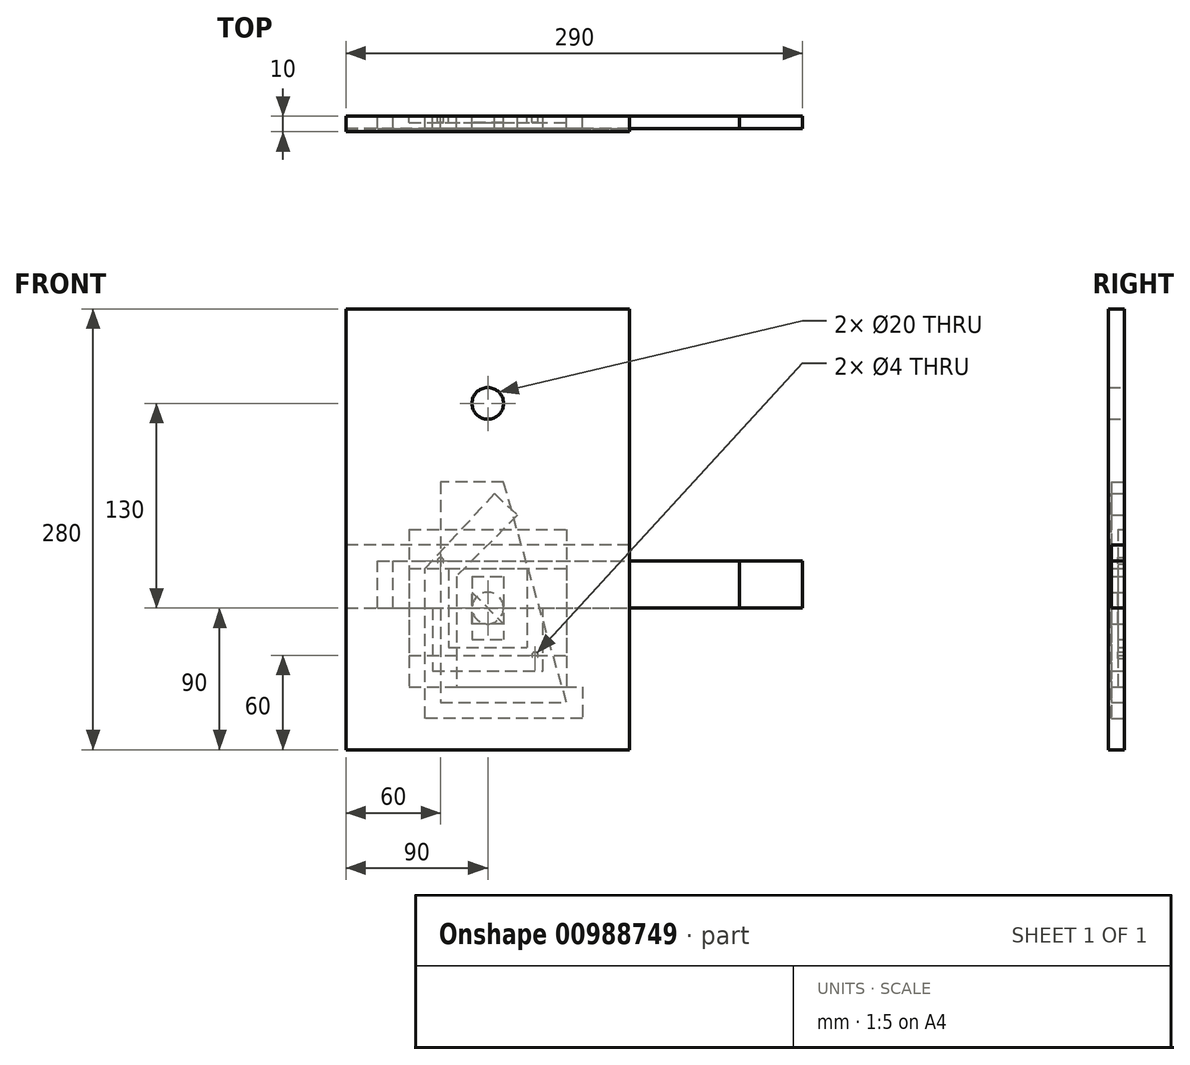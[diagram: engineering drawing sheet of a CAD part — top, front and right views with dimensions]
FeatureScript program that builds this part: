
annotation { "Feature Type Name" : "Feature", "Feature Type Description" : "" }
export const myFeature = defineFeature(function(context is Context, id is Id, definition is map)
    precondition{}
    {
        {
            var Q0;
            Q0=qCreatedBy(makeId("Front.planeOp"),FACE);
            var sketch = newSketch(context, id + "F0", { "sketchPlane" : qUnion([Q0])});
            skLineSegment(sketch, "E0", {"start": v(-30, -60) * mm, "end": v(50, -60) * mm});
            skLineSegment(sketch, "E1", {"start": v(50, -60) * mm, "end": v(10, 80) * mm});
            skLineSegment(sketch, "E2", {"start": v(10, 80) * mm, "end": v(-30, 80) * mm});
            skLineSegment(sketch, "E3", {"start": v(-30, 80) * mm, "end": v(-30, -60) * mm});
            skSolve(sketch);
        }
        {
            var Q0;
            Q0=makeQuery(id+"F0.imprint","IMPRINT",FACE,{"disambiguationData":[TD([[makeQuery(id+"F0.imprint","IMPRINT",EDGE,{"derivedFrom":sQuery(id+"F0.wireOp",EDGE,"E0")}),1.0]])]});
            extrude(context, id + "F1", {"entities" : qUnion([Q0]), "depth" : 8 * mm, "offsetDistance" : 25 * mm});
        }
        {
            var Q0;
            Q0=qCreatedBy(makeId("Front.planeOp"),FACE);
            var sketch = newSketch(context, id + "F2", { "sketchPlane" : qUnion([Q0])});
            skLineSegment(sketch, "E4.bottom", {"start": v(-60, 0) * mm, "end": v(160, 0) * mm});
            skLineSegment(sketch, "E4.top", {"start": v(-60, 30) * mm, "end": v(160, 30) * mm});
            skLineSegment(sketch, "E4.left", {"start": v(-60, 0) * mm, "end": v(-60, 30) * mm});
            skLineSegment(sketch, "E4.right", {"start": v(160, 0) * mm, "end": v(160, 30) * mm});
            skSolve(sketch);
        }
        {
            var Q0;
            Q0=makeQuery(id+"F2.imprint","IMPRINT",FACE,{"disambiguationData":[TD([[makeQuery(id+"F2.imprint","IMPRINT",EDGE,{"derivedFrom":sQuery(id+"F2.wireOp",EDGE,"E4.bottom")}),1.0]])]});
            extrude(context, id + "F3", {"entities" : qUnion([Q0]), "depth" : 8 * mm, "offsetDistance" : 25 * mm});
        }
        {
            var Q0;
            Q0=qCreatedBy(makeId("Front.planeOp"),FACE);
            var sketch = newSketch(context, id + "F4", { "sketchPlane" : qUnion([Q0])});
            skLineSegment(sketch, "E5.bottom", {"start": v(-70, 0) * mm, "end": v(200, 0) * mm});
            skLineSegment(sketch, "E5.top", {"start": v(-70, 30) * mm, "end": v(200, 30) * mm});
            skLineSegment(sketch, "E5.left", {"start": v(-70, 0) * mm, "end": v(-70, 30) * mm});
            skLineSegment(sketch, "E5.right", {"start": v(200, 0) * mm, "end": v(200, 30) * mm});
            skSolve(sketch);
        }
        {
            var Q0;
            Q0=makeQuery(id+"F4.imprint","IMPRINT",FACE,{"disambiguationData":[TD([[makeQuery(id+"F4.imprint","IMPRINT",EDGE,{"derivedFrom":sQuery(id+"F4.wireOp",EDGE,"E5.bottom")}),1.0]])]});
            extrude(context, id + "F5", {"entities" : qUnion([Q0]), "depth" : 8 * mm, "offsetDistance" : 25 * mm});
        }
        {
            var Q0;
            Q0=qCreatedBy(makeId("Front.planeOp"),FACE);
            var sketch = newSketch(context, id + "F6", { "sketchPlane" : qUnion([Q0])});
            skLineSegment(sketch, "E6.bottom", {"start": v(-90, 190) * mm, "end": v(90, 190) * mm});
            skLineSegment(sketch, "E6.top", {"start": v(-90, -90) * mm, "end": v(90, -90) * mm});
            skLineSegment(sketch, "E6.left", {"start": v(-90, 190) * mm, "end": v(-90, -90) * mm});
            skLineSegment(sketch, "E6.right", {"start": v(90, 190) * mm, "end": v(90, -90) * mm});
            skCircle(sketch, "E7", {"center": v(0, 130) * mm, "radius": 10 * mm});
            skSolve(sketch);
        }
        {
            var Q0;
            Q0=makeQuery(id+"F6.imprint","IMPRINT",FACE,{"disambiguationData":[TD([[makeQuery(id+"F6.imprint","IMPRINT",EDGE,{"derivedFrom":sQuery(id+"F6.wireOp",EDGE,"E6.bottom")}),-1.0]])]});
            extrude(context, id + "F7", {"entities" : qUnion([Q0]), "depth" : 10 * mm, "offsetDistance" : 25 * mm});
        }
        {
            var Q0;
            Q0=qCreatedBy(makeId("Front.planeOp"),FACE);
            var sketch = newSketch(context, id + "F8", { "sketchPlane" : qUnion([Q0])});
            skLineSegment(sketch, "E8.bottom", {"start": v(-50, 25) * mm, "end": v(50, 25) * mm});
            skLineSegment(sketch, "E8.top", {"start": v(-50, -30) * mm, "end": v(50, -30) * mm});
            skLineSegment(sketch, "E8.left", {"start": v(-50, 25) * mm, "end": v(-50, -30) * mm});
            skLineSegment(sketch, "E8.right", {"start": v(50, 25) * mm, "end": v(50, -30) * mm});
            skSolve(sketch);
        }
        {
            var Q0;
            Q0=makeQuery(id+"F8.imprint","IMPRINT",FACE,{"disambiguationData":[TD([[makeQuery(id+"F8.imprint","IMPRINT",EDGE,{"derivedFrom":sQuery(id+"F8.wireOp",EDGE,"E8.bottom")}),-1.0]])]});
            extrude(context, id + "F9", {"entities" : qUnion([Q0]), "depth" : 4 * mm, "offsetDistance" : 25 * mm});
        }
        {
            var Q0;
            Q0=qCreatedBy(makeId("Front.planeOp"),FACE);
            var sketch = newSketch(context, id + "F10", { "sketchPlane" : qUnion([Q0])});
            skLineSegment(sketch, "E9.bottom", {"start": v(-50, 50) * mm, "end": v(50, 50) * mm});
            skLineSegment(sketch, "E9.top", {"start": v(-50, -50) * mm, "end": v(50, -50) * mm});
            skLineSegment(sketch, "E9.left", {"start": v(-50, 50) * mm, "end": v(-50, -50) * mm});
            skLineSegment(sketch, "E9.right", {"start": v(50, 50) * mm, "end": v(50, -50) * mm});
            skCircle(sketch, "E10", {"center": v(0, 0) * mm, "radius": 10 * mm});
            skCircle(sketch, "E11", {"center": v(-30, 30) * mm, "radius": 2 * mm});
            skCircle(sketch, "E12", {"center": v(30, -30) * mm, "radius": 2 * mm});
            skSolve(sketch);
        }
        {
            var Q0;
            Q0=makeQuery(id+"F10.imprint","IMPRINT",FACE,{"disambiguationData":[TD([[makeQuery(id+"F10.imprint","IMPRINT",EDGE,{"derivedFrom":sQuery(id+"F10.wireOp",EDGE,"E9.bottom")}),-1.0]])]});
            extrude(context, id + "F11", {"entities" : qUnion([Q0]), "depth" : 4 * mm, "offsetDistance" : 25 * mm});
        }
        {
            var Q0;
            Q0=qCreatedBy(makeId("Front.planeOp"),FACE);
            var sketch = newSketch(context, id + "F12", { "sketchPlane" : qUnion([Q0])});
            skLineSegment(sketch, "E13", {"start": v(-35, -40) * mm, "end": v(35, -40) * mm});
            skLineSegment(sketch, "E14", {"start": v(35, -40) * mm, "end": v(35, 0) * mm});
            skLineSegment(sketch, "E15", {"start": v(35, 0) * mm, "end": v(90, 0) * mm});
            skLineSegment(sketch, "E16", {"start": v(90, 0) * mm, "end": v(90, 40) * mm});
            skLineSegment(sketch, "E17", {"start": v(90, 40) * mm, "end": v(-90, 40) * mm});
            skLineSegment(sketch, "E18", {"start": v(-90, 40) * mm, "end": v(-90, 0) * mm});
            skLineSegment(sketch, "E19", {"start": v(-90, 0) * mm, "end": v(-35, 0) * mm});
            skLineSegment(sketch, "E20", {"start": v(-35, 0) * mm, "end": v(-35, -40) * mm});
            skSolve(sketch);
        }
        {
            var Q0;
            Q0=makeQuery(id+"F12.imprint","IMPRINT",FACE,{"disambiguationData":[TD([[makeQuery(id+"F12.imprint","IMPRINT",EDGE,{"derivedFrom":sQuery(id+"F12.wireOp",EDGE,"E13")}),1.0]])]});
            extrude(context, id + "F13", {"entities" : qUnion([Q0]), "depth" : 8 * mm, "offsetDistance" : 25 * mm});
        }
        {
            var Q0;
            Q0=qCreatedBy(makeId("Front.planeOp"),FACE);
            var sketch = newSketch(context, id + "F14", { "sketchPlane" : qUnion([Q0])});
            skLineSegment(sketch, "E21", {"start": v(60, -50) * mm, "end": v(60, -70) * mm});
            skLineSegment(sketch, "E22", {"start": v(60, -70) * mm, "end": v(-40, -70) * mm});
            skLineSegment(sketch, "E23", {"start": v(-40, -70) * mm, "end": v(-40, 25) * mm});
            skLineSegment(sketch, "E24", {"start": v(-40, 25) * mm, "end": v(4.24, 72.62) * mm});
            skLineSegment(sketch, "E25", {"start": v(4.24, 72.62) * mm, "end": v(18.9, 59.01) * mm});
            skLineSegment(sketch, "E26", {"start": v(18.9, 59.01) * mm, "end": v(-20, 20.12) * mm});
            skLineSegment(sketch, "E27", {"start": v(-20, 20.12) * mm, "end": v(-20, -50) * mm});
            skLineSegment(sketch, "E28", {"start": v(-20, -50) * mm, "end": v(60, -50) * mm});
            skSolve(sketch);
        }
        {
            var Q0;
            Q0=makeQuery(id+"F14.imprint","IMPRINT",FACE,{"disambiguationData":[TD([[makeQuery(id+"F14.imprint","IMPRINT",EDGE,{"derivedFrom":sQuery(id+"F14.wireOp",EDGE,"E21")}),-1.0]])]});
            extrude(context, id + "F15", {"entities" : qUnion([Q0]), "depth" : 8 * mm, "offsetDistance" : 25 * mm});
        }
        {
            var Q0;
            Q0=qCreatedBy(makeId("Front.planeOp"),FACE);
            var sketch = newSketch(context, id + "F16", { "sketchPlane" : qUnion([Q0])});
            skLineSegment(sketch, "E29.bottom", {"start": v(-25, 25) * mm, "end": v(25, 25) * mm});
            skLineSegment(sketch, "E29.top", {"start": v(-25, -25) * mm, "end": v(25, -25) * mm});
            skLineSegment(sketch, "E29.left", {"start": v(-25, 25) * mm, "end": v(-25, -25) * mm});
            skLineSegment(sketch, "E29.right", {"start": v(25, 25) * mm, "end": v(25, -25) * mm});
            skSolve(sketch);
        }
        {
            var Q0;
            Q0=makeQuery(id+"F16.imprint","IMPRINT",FACE,{"disambiguationData":[TD([[makeQuery(id+"F16.imprint","IMPRINT",EDGE,{"derivedFrom":sQuery(id+"F16.wireOp",EDGE,"E29.bottom")}),-1.0]])]});
            extrude(context, id + "F17", {"entities" : qUnion([Q0]), "depth" : 4 * mm, "offsetDistance" : 25 * mm});
        }
        {
            var Q0;
            Q0=qCreatedBy(makeId("Front.planeOp"),FACE);
            var sketch = newSketch(context, id + "F18", { "sketchPlane" : qUnion([Q0])});
            skLineSegment(sketch, "E30", {"start": v(-10, -10) * mm, "end": v(-10, 10) * mm});
            skLineSegment(sketch, "E31", {"start": v(-10, 10) * mm, "end": v(10, -10) * mm});
            skLineSegment(sketch, "E32", {"start": v(10, -10) * mm, "end": v(-10, -10) * mm});
            skSolve(sketch);
        }
        {
            var Q0;
            Q0=makeQuery(id+"F18.imprint","IMPRINT",FACE,{"disambiguationData":[TD([[makeQuery(id+"F18.imprint","IMPRINT",EDGE,{"derivedFrom":sQuery(id+"F18.wireOp",EDGE,"E30")}),-1.0]])]});
            extrude(context, id + "F19", {"entities" : qUnion([Q0]), "depth" : 8 * mm, "offsetDistance" : 25 * mm});
        }
        {
            var Q0;
            Q0=qCreatedBy(makeId("Front.planeOp"),FACE);
            var sketch = newSketch(context, id + "F20", { "sketchPlane" : qUnion([Q0])});
            skLineSegment(sketch, "E33.bottom", {"start": v(-10, 20) * mm, "end": v(10, 20) * mm});
            skLineSegment(sketch, "E33.top", {"start": v(-10, -20) * mm, "end": v(10, -20) * mm});
            skLineSegment(sketch, "E33.left", {"start": v(-10, 20) * mm, "end": v(-10, -20) * mm});
            skLineSegment(sketch, "E33.right", {"start": v(10, 20) * mm, "end": v(10, -20) * mm});
            skSolve(sketch);
        }
        {
            var Q0;
            Q0=makeQuery(id+"F20.imprint","IMPRINT",FACE,{"disambiguationData":[TD([[makeQuery(id+"F20.imprint","IMPRINT",EDGE,{"derivedFrom":sQuery(id+"F20.wireOp",EDGE,"E33.bottom")}),-1.0]])]});
            extrude(context, id + "F21", {"entities" : qUnion([Q0]), "depth" : 4 * mm, "offsetDistance" : 25 * mm});
        }
    });
